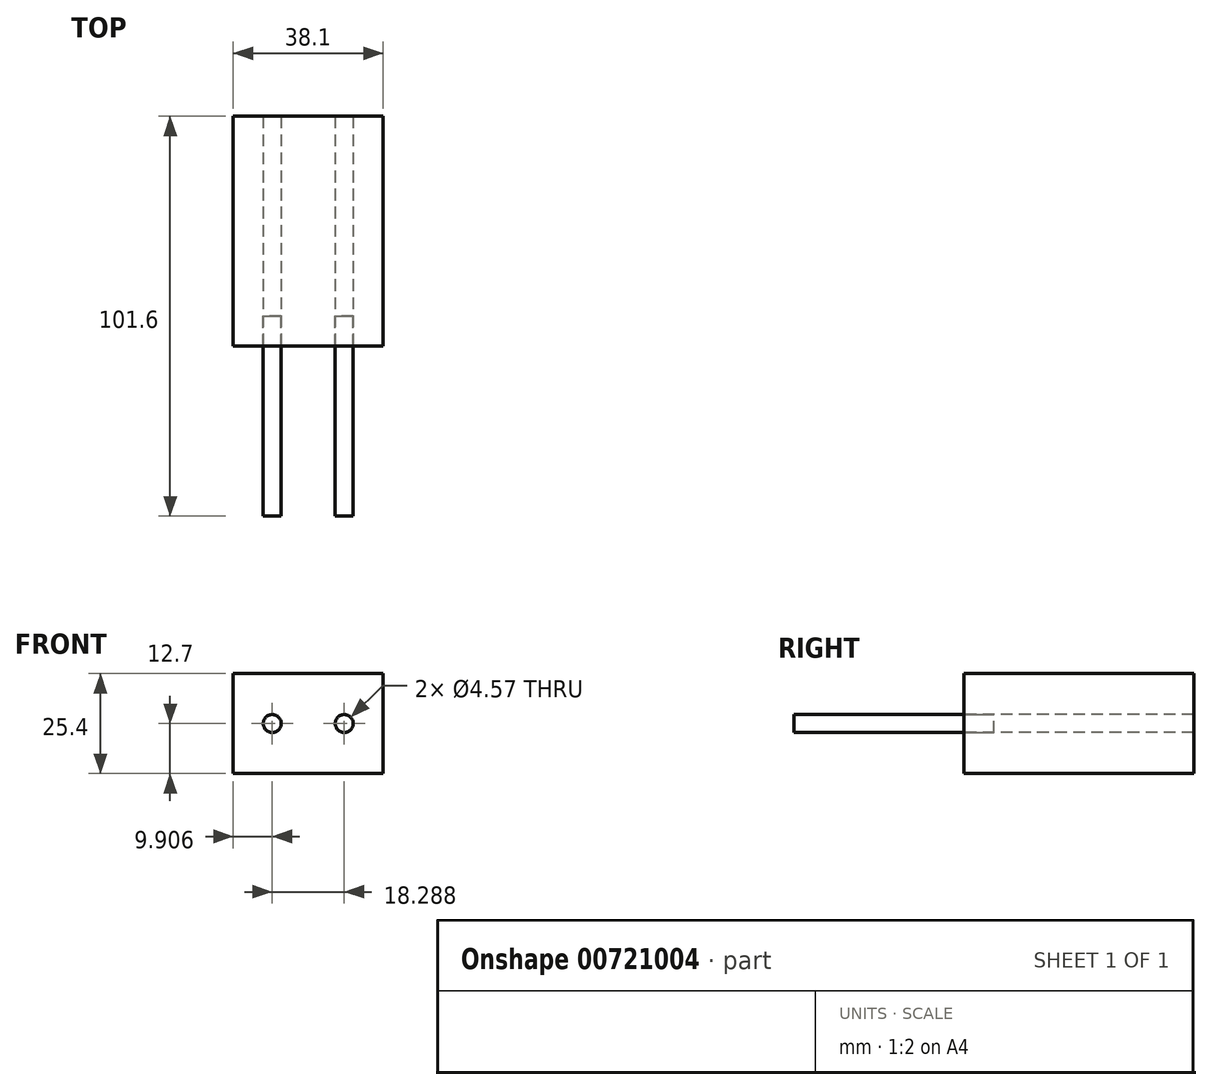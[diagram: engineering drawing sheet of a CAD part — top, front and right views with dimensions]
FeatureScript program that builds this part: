
annotation { "Feature Type Name" : "Feature", "Feature Type Description" : "" }
export const myFeature = defineFeature(function(context is Context, id is Id, definition is map)
    precondition{}
    {
        {
            var Q0;
            Q0=qCreatedBy(makeId("Front.planeOp"),FACE);
            var sketch = newSketch(context, id + "F0", { "sketchPlane" : qUnion([Q0])});
            skLineSegment(sketch, "E0.bottom", {"start": v(0, 0) * mm, "end": v(38.1, 0) * mm});
            skLineSegment(sketch, "E0.top", {"start": v(0, 25.4) * mm, "end": v(38.1, 25.4) * mm});
            skLineSegment(sketch, "E0.left", {"start": v(0, 0) * mm, "end": v(0, 25.4) * mm});
            skLineSegment(sketch, "E0.right", {"start": v(38.1, 0) * mm, "end": v(38.1, 25.4) * mm});
            skCircle(sketch, "E1", {"center": v(9.9, 12.7) * mm, "radius": 2.29 * mm});
            skCircle(sketch, "E2", {"center": v(28.2, 12.7) * mm, "radius": 2.29 * mm});
            skSolve(sketch);
        }
        {
            var Q0;
            Q0=makeQuery(id+"F0.imprint","IMPRINT",FACE,{"disambiguationData":[TD([[makeQuery(id+"F0.imprint","IMPRINT",EDGE,{"derivedFrom":sQuery(id+"F0.wireOp",EDGE,"E1")}),1.0]])]});
            var Q1;
            Q1=makeQuery(id+"F0.imprint","IMPRINT",FACE,{"disambiguationData":[TD([[makeQuery(id+"F0.imprint","IMPRINT",EDGE,{"derivedFrom":sQuery(id+"F0.wireOp",EDGE,"E2")}),1.0]])]});
            extrude(context, id + "F1", {"entities" : qUnion([Q0, Q1]), "depth" : 50.8 * mm, "offsetDistance" : 25.4 * mm});
        }
        {
            var Q0;
            Q0=makeQuery(id+"F0.imprint","IMPRINT",FACE,{"disambiguationData":[TD([[makeQuery(id+"F0.imprint","IMPRINT",EDGE,{"derivedFrom":sQuery(id+"F0.wireOp",EDGE,"E0.bottom")}),1.0]])]});
            extrude(context, id + "F2", {"entities" : qUnion([Q0]), "oppositeDirection" : true, "depth" : 50.8 * mm, "offsetDistance" : 25.4 * mm, "hasSecondDirection" : true, "secondDirectionOppositeDirection" : false, "secondDirectionDepth" : 7.62 * mm});
        }
    });
